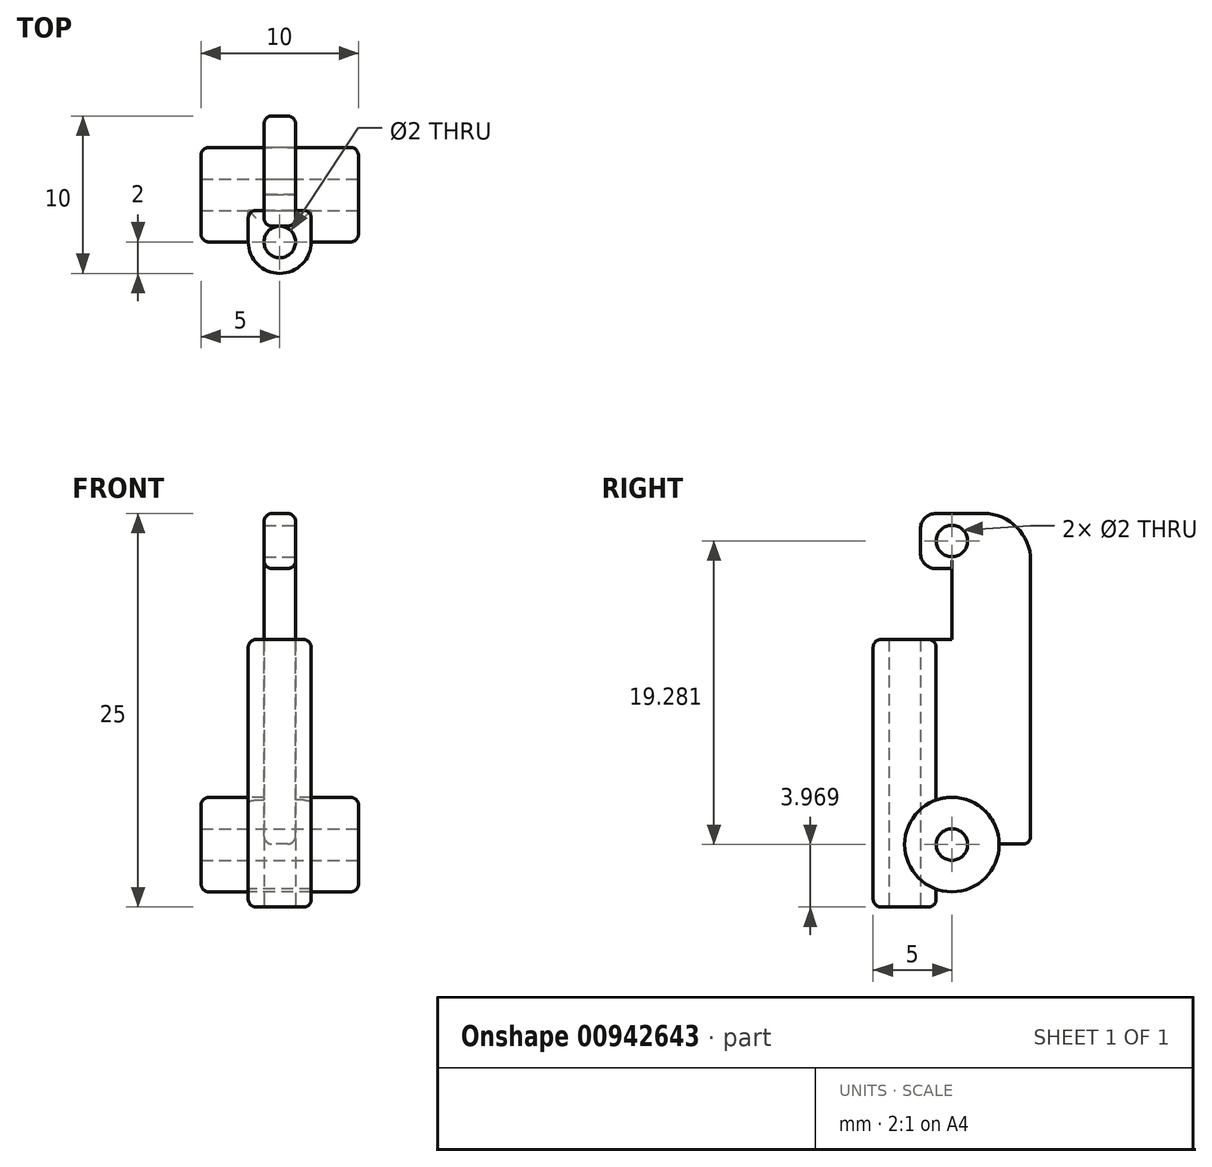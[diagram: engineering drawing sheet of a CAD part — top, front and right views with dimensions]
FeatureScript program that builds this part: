
annotation { "Feature Type Name" : "Feature", "Feature Type Description" : "" }
export const myFeature = defineFeature(function(context is Context, id is Id, definition is map)
    precondition{}
    {
        {
            var Q0;
            Q0=qCreatedBy(makeId("Front.planeOp"),FACE);
            var sketch = newSketch(context, id + "F0", { "sketchPlane" : qUnion([Q0])});
            skLineSegment(sketch, "E0.bottom", {"start": v(2, -8.5) * mm, "end": v(-2, -8.5) * mm});
            skLineSegment(sketch, "E0.top", {"start": v(2, 8.5) * mm, "end": v(-2, 8.5) * mm});
            skLineSegment(sketch, "E0.left", {"start": v(2, -8.5) * mm, "end": v(2, 8.5) * mm});
            skLineSegment(sketch, "E0.right", {"start": v(-2, -8.5) * mm, "end": v(-2, 8.5) * mm});
            skPoint(sketch, "E0.middle", {"position": v(0, 0) * mm});
            skSolve(sketch);
        }
        {
            var Q0;
            Q0 = qSketchRegion(id + "F0", true);
            extrude(context, id + "F1", {"entities" : qUnion([Q0]), "depth" : 4 * mm, "offsetDistance" : 25 * mm});
        }
        {
            var Q0;
            Q0=qCreatedBy(makeId("Right.planeOp"),FACE);
            var sketch = newSketch(context, id + "F2", { "sketchPlane" : qUnion([Q0])});
            skLineSegment(sketch, "E1.bottom", {"start": v(0, -4.5) * mm, "end": v(6, -4.5) * mm});
            skLineSegment(sketch, "E1.top", {"start": v(0, 16.5) * mm, "end": v(6, 16.5) * mm});
            skLineSegment(sketch, "E1.left", {"start": v(0, -4.5) * mm, "end": v(0, 16.5) * mm});
            skLineSegment(sketch, "E1.right", {"start": v(6, -4.5) * mm, "end": v(6, 16.5) * mm});
            skSolve(sketch);
        }
        {
            var Q0;
            Q0 = qSketchRegion(id + "F2", true);
            extrude(context, id + "F3", {"entities" : qUnion([Q0]), "operationType" : NewBodyOperationType.ADD, "depth" : 1 * mm, "offsetDistance" : 25 * mm});
        }
        {
            var Q0;
            Q0=qCreatedBy(makeId("Right.planeOp"),FACE);
            var sketch = newSketch(context, id + "F4", { "sketchPlane" : qUnion([Q0])});
            skLineSegment(sketch, "E2.bottom", {"start": v(0, -4.5) * mm, "end": v(6, -4.5) * mm});
            skLineSegment(sketch, "E2.top", {"start": v(0, 16.5) * mm, "end": v(6, 16.5) * mm});
            skLineSegment(sketch, "E2.left", {"start": v(0, -4.5) * mm, "end": v(0, 16.5) * mm});
            skLineSegment(sketch, "E2.right", {"start": v(6, -4.5) * mm, "end": v(6, 16.5) * mm});
            skSolve(sketch);
        }
        {
            var Q0;
            Q0 = qSketchRegion(id + "F4", true);
            extrude(context, id + "F5", {"entities" : qUnion([Q0]), "operationType" : NewBodyOperationType.ADD, "oppositeDirection" : true, "depth" : 1 * mm, "offsetDistance" : 25 * mm});
        }
        {
            var Q0;
            Q0=qCreatedBy(makeId("Right.planeOp"),FACE);
            var sketch = newSketch(context, id + "F6", { "sketchPlane" : qUnion([Q0])});
            skCircle(sketch, "E3", {"center": v(1, -4.53) * mm, "radius": 3 * mm});
            skSolve(sketch);
        }
        {
            var Q0;
            Q0=makeQuery(id+"F6.imprint","IMPRINT",FACE,{"disambiguationData":[TD([[makeQuery(id+"F6.imprint","IMPRINT",EDGE,{"derivedFrom":sQuery(id+"F6.wireOp",EDGE,"E3")}),1.0]])]});
            extrude(context, id + "F7", {"entities" : qUnion([Q0]), "operationType" : NewBodyOperationType.ADD, "depth" : 5 * mm, "offsetDistance" : 25 * mm});
        }
        {
            var Q0;
            Q0=makeQuery(id+"F7.opExtrude","CAP_FACE",FACE,{"disambiguationData":[OSD([sQuery(id+"F6.wireOp",EDGE,"E3")])],"isStart":false});
            extrude(context, id + "F8", {"entities" : qUnion([Q0]), "operationType" : NewBodyOperationType.ADD, "oppositeDirection" : true, "depth" : 10 * mm, "offsetDistance" : 25 * mm});
        }
        {
            var Q0;
            Q0=makeQuery(id+"F5.boolean.opBoolean","MERGE",FACE,{"derivedFrom":[makeQuery(id+"F3.opExtrude","SWEPT_FACE",FACE,{"disambiguationData":[OSD([sQuery(id+"F2.wireOp",EDGE,"E1.left")])]}),makeQuery(id+"F5.opExtrude","SWEPT_FACE",FACE,{"disambiguationData":[OSD([sQuery(id+"F4.wireOp",EDGE,"E2.left")])]})]});
            var sketch = newSketch(context, id + "F9", { "sketchPlane" : qUnion([Q0])});
            skLineSegment(sketch, "E4.bottom", {"start": v(-1, 8.5) * mm, "end": v(1, 8.5) * mm});
            skLineSegment(sketch, "E4.top", {"start": v(-1, 13) * mm, "end": v(1, 13) * mm});
            skLineSegment(sketch, "E4.left", {"start": v(-1, 8.5) * mm, "end": v(-1, 13) * mm});
            skLineSegment(sketch, "E4.right", {"start": v(1, 8.5) * mm, "end": v(1, 13) * mm});
            skSolve(sketch);
        }
        {
            var Q0;
            Q0 = qSketchRegion(id + "F9", true);
            extrude(context, id + "F10", {"entities" : qUnion([Q0]), "operationType" : NewBodyOperationType.REMOVE, "oppositeDirection" : true, "depth" : 1 * mm, "offsetDistance" : 25 * mm});
        }
        {
            var Q0;
            Q0=makeQuery(id+"F5.boolean.opBoolean","MERGE",FACE,{"derivedFrom":[makeQuery(id+"F3.opExtrude","SWEPT_FACE",FACE,{"disambiguationData":[OSD([sQuery(id+"F2.wireOp",EDGE,"E1.left")])]}),makeQuery(id+"F5.opExtrude","SWEPT_FACE",FACE,{"disambiguationData":[OSD([sQuery(id+"F4.wireOp",EDGE,"E2.left")])]})]});
            extrude(context, id + "F11", {"entities" : qUnion([Q0]), "operationType" : NewBodyOperationType.ADD, "depth" : 1 * mm, "offsetDistance" : 25 * mm});
        }
        {
            var Q0;
            Q0=makeQuery(id+"F5.boolean.opBoolean","MERGE",EDGE,{"derivedFrom":[makeQuery(id+"F3.opExtrude","SWEPT_EDGE",EDGE,{"disambiguationData":[OSD([sQuery(id+"F2.wireOp",EDGE,"E1.top"),sQuery(id+"F2.wireOp",EDGE,"E1.right")])]}),makeQuery(id+"F5.opExtrude","SWEPT_EDGE",EDGE,{"disambiguationData":[OSD([sQuery(id+"F4.wireOp",EDGE,"E2.top"),sQuery(id+"F4.wireOp",EDGE,"E2.right")])]})]});
            fillet(context, id + "F12", {"entities" : qUnion([Q0]), "radius" : 3 * mm, "tangentPropagation" : true, "allowEdgeOverflow" : false});
        }
        {
            var Q0;
            Q0=makeQuery(id+"F11.opExtrude","CAP_EDGE",EDGE,{"disambiguationData":[OSD([sQuery(id+"F9.wireOp",EDGE,"E4.top")])],"isStart":false});
            var Q1;
            Q1=makeQuery(id+"F11.opExtrude","CAP_EDGE",EDGE,{"disambiguationData":[OSD([sQuery(id+"F2.wireOp",EDGE,"E1.top"),sQuery(id+"F2.wireOp",EDGE,"E1.left"),sQuery(id+"F4.wireOp",EDGE,"E2.top"),sQuery(id+"F4.wireOp",EDGE,"E2.left")])],"isStart":false});
            fillet(context, id + "F13", {"entities" : qUnion([Q0, Q1]), "radius" : 1 * mm, "tangentPropagation" : true, "allowEdgeOverflow" : false});
        }
        {
            var Q0;
            Q0=makeQuery(id+"F1.opExtrude","CAP_EDGE",EDGE,{"disambiguationData":[OSD([sQuery(id+"F0.wireOp",EDGE,"E0.left")])],"isStart":false});
            var Q1;
            Q1=makeQuery(id+"F1.opExtrude","CAP_EDGE",EDGE,{"disambiguationData":[OSD([sQuery(id+"F0.wireOp",EDGE,"E0.right")])],"isStart":false});
            fillet(context, id + "F14", {"entities" : qUnion([Q0, Q1]), "radius" : 2 * mm, "tangentPropagation" : true, "allowEdgeOverflow" : false});
        }
        {
            var Q0;
            Q0=makeQuery(id+"F14.opFillet","BLEND_EDGE",EDGE,{"blendedFrom":[makeQuery(id+"F1.opExtrude","CAP_EDGE",EDGE,{"disambiguationData":[OSD([sQuery(id+"F0.wireOp",EDGE,"E0.left")])],"isStart":false}),makeQuery(id+"F10.boolean.opBoolean","MERGE",FACE,{"derivedFrom":[makeQuery(id+"F1.opExtrude","SWEPT_FACE",FACE,{"disambiguationData":[OSD([sQuery(id+"F0.wireOp",EDGE,"E0.top")])]})],"fromTools":[makeQuery(id+"F10.opExtrude","SWEPT_FACE",FACE,{"disambiguationData":[OSD([sQuery(id+"F9.wireOp",EDGE,"E4.bottom")])]})]})],"blendedInto":[makeQuery(id+"F10.boolean.opBoolean","MERGE",FACE,{"derivedFrom":[makeQuery(id+"F1.opExtrude","SWEPT_FACE",FACE,{"disambiguationData":[OSD([sQuery(id+"F0.wireOp",EDGE,"E0.top")])]})],"fromTools":[makeQuery(id+"F10.opExtrude","SWEPT_FACE",FACE,{"disambiguationData":[OSD([sQuery(id+"F9.wireOp",EDGE,"E4.bottom")])]})]})]});
            var Q1;
            Q1=makeQuery(id+"F10.boolean.opBoolean","COPY",EDGE,{"derivedFrom":makeQuery(id+"F10.opExtrude","CAP_EDGE",EDGE,{"disambiguationData":[OSD([sQuery(id+"F9.wireOp",EDGE,"E4.right")])],"isStart":false})});
            var Q2;
            Q2=makeQuery(id+"F10.boolean.opBoolean","COPY",EDGE,{"derivedFrom":makeQuery(id+"F10.opExtrude","CAP_EDGE",EDGE,{"disambiguationData":[OSD([sQuery(id+"F9.wireOp",EDGE,"E4.left")])],"isStart":false})});
            var Q3;
            {var subQ0=sQuery(id+"F0.wireOp",EDGE,"E0.left");var subQ1=sQuery(id+"F0.wireOp",EDGE,"E0.top");Q3=makeQuery(id+"F7.boolean.opBoolean","SPLIT",EDGE,{"disambiguationData":[TD([makeQuery(id+"F1.opExtrude","SWEPT_FACE",FACE,{"disambiguationData":[OSD([subQ1])]})])],"derivedFrom":makeQuery(id+"F1.opExtrude","CAP_EDGE",EDGE,{"disambiguationData":[OSD([subQ0])],"isStart":true})});}
            var Q4;
            {var subQ0=sQuery(id+"F0.wireOp",EDGE,"E0.right");var subQ1=sQuery(id+"F0.wireOp",EDGE,"E0.top");Q4=makeQuery(id+"F8.boolean.opBoolean","SPLIT",EDGE,{"disambiguationData":[TD([makeQuery(id+"F1.opExtrude","SWEPT_FACE",FACE,{"disambiguationData":[OSD([subQ1])]})])],"derivedFrom":makeQuery(id+"F1.opExtrude","CAP_EDGE",EDGE,{"disambiguationData":[OSD([subQ0])],"isStart":true})});}
            var Q5;
            Q5=makeQuery(id+"F14.opFillet","BLEND_EDGE",EDGE,{"blendedFrom":[makeQuery(id+"F1.opExtrude","CAP_EDGE",EDGE,{"disambiguationData":[OSD([sQuery(id+"F0.wireOp",EDGE,"E0.left")])],"isStart":false}),makeQuery(id+"F1.opExtrude","SWEPT_FACE",FACE,{"disambiguationData":[OSD([sQuery(id+"F0.wireOp",EDGE,"E0.bottom")])]})],"blendedInto":[makeQuery(id+"F1.opExtrude","SWEPT_FACE",FACE,{"disambiguationData":[OSD([sQuery(id+"F0.wireOp",EDGE,"E0.bottom")])]})]});
            var Q6;
            Q6=makeQuery(id+"F1.opExtrude","SWEPT_EDGE",EDGE,{"disambiguationData":[OSD([sQuery(id+"F0.wireOp",EDGE,"E0.bottom"),sQuery(id+"F0.wireOp",EDGE,"E0.left")])]});
            var Q7;
            Q7=makeQuery(id+"F1.opExtrude","CAP_EDGE",EDGE,{"disambiguationData":[OSD([sQuery(id+"F0.wireOp",EDGE,"E0.bottom")])],"isStart":true});
            fillet(context, id + "F15", {"entities" : qUnion([Q0, Q1, Q2, Q3, Q4, Q5, Q6, Q7]), "radius" : .5 * mm, "tangentPropagation" : true, "allowEdgeOverflow" : false});
        }
        {
            var Q0;
            Q0=makeQuery(id+"F5.opExtrude","CAP_EDGE",EDGE,{"disambiguationData":[OSD([sQuery(id+"F4.wireOp",EDGE,"E2.right")])],"isStart":false});
            var Q1;
            Q1=makeQuery(id+"F3.opExtrude","CAP_EDGE",EDGE,{"disambiguationData":[OSD([sQuery(id+"F2.wireOp",EDGE,"E1.right")])],"isStart":false});
            var Q2;
            Q2=makeQuery(id+"F10.boolean.opBoolean","COPY",EDGE,{"derivedFrom":makeQuery(id+"F10.opExtrude","SWEPT_EDGE",EDGE,{"disambiguationData":[OSD([sQuery(id+"F9.wireOp",EDGE,"E4.bottom"),sQuery(id+"F9.wireOp",EDGE,"E4.left")])]})});
            var Q3;
            Q3=makeQuery(id+"F10.boolean.opBoolean","COPY",EDGE,{"derivedFrom":makeQuery(id+"F10.opExtrude","SWEPT_EDGE",EDGE,{"disambiguationData":[OSD([sQuery(id+"F9.wireOp",EDGE,"E4.bottom"),sQuery(id+"F9.wireOp",EDGE,"E4.right")])]})});
            var Q4;
            {var subQ1=sQuery(id+"F0.wireOp",EDGE,"E0.top");var subQ2=makeQuery(id+"F1.opExtrude","SWEPT_FACE",FACE,{"disambiguationData":[OSD([subQ1])]});var subQ3=sQuery(id+"F0.wireOp",EDGE,"E0.left");var subQ4=makeQuery(id+"F1.opExtrude","CAP_FACE",FACE,{"disambiguationData":[OSD([sQuery(id+"F0.wireOp",EDGE,"E0.bottom"),subQ1,subQ3,sQuery(id+"F0.wireOp",EDGE,"E0.right")])],"isStart":true});Q4=makeQuery(id+"F3.boolean.opBoolean","SPLIT",EDGE,{"disambiguationData":[topologyDisambiguationEdgeConnected([subQ4,subQ2]),TD([makeQuery(id+"F1.opExtrude","SWEPT_FACE",FACE,{"disambiguationData":[OSD([subQ3])]})])],"derivedFrom":makeQuery(id+"F1.opExtrude","CAP_EDGE",EDGE,{"disambiguationData":[OSD([subQ1])],"isStart":true})});}
            var Q5;
            {var subQ1=sQuery(id+"F0.wireOp",EDGE,"E0.right");var subQ2=sQuery(id+"F0.wireOp",EDGE,"E0.top");var subQ3=makeQuery(id+"F1.opExtrude","SWEPT_FACE",FACE,{"disambiguationData":[OSD([subQ2])]});var subQ4=makeQuery(id+"F1.opExtrude","CAP_FACE",FACE,{"disambiguationData":[OSD([sQuery(id+"F0.wireOp",EDGE,"E0.bottom"),subQ2,sQuery(id+"F0.wireOp",EDGE,"E0.left"),subQ1])],"isStart":true});Q5=makeQuery(id+"F5.boolean.opBoolean","SPLIT",EDGE,{"derivedFrom":makeQuery(id+"F3.boolean.opBoolean","SPLIT",EDGE,{"disambiguationData":[topologyDisambiguationEdgeConnected([subQ4,subQ3]),TD([makeQuery(id+"F1.opExtrude","SWEPT_FACE",FACE,{"disambiguationData":[OSD([subQ1])]})])],"derivedFrom":makeQuery(id+"F1.opExtrude","CAP_EDGE",EDGE,{"disambiguationData":[OSD([subQ2])],"isStart":true})})});}
            fillet(context, id + "F16", {"entities" : qUnion([Q0, Q1, Q2, Q3, Q4, Q5]), "radius" : .5 * mm, "tangentPropagation" : true, "allowEdgeOverflow" : false});
        }
        {
            var Q0;
            Q0=makeQuery(id+"F5.opExtrude","CAP_EDGE",EDGE,{"disambiguationData":[OSD([sQuery(id+"F4.wireOp",EDGE,"E2.bottom")])],"isStart":false});
            var Q1;
            Q1=makeQuery(id+"F8.opExtrude","CAP_EDGE",EDGE,{"disambiguationData":[OSD([sQuery(id+"F6.wireOp",EDGE,"E3")])],"isStart":false});
            fillet(context, id + "F17", {"entities" : qUnion([Q0, Q1]), "radius" : .5 * mm, "tangentPropagation" : true, "allowEdgeOverflow" : false});
        }
        {
            var Q0;
            Q0=makeQuery(id+"F7.opExtrude","CAP_EDGE",EDGE,{"disambiguationData":[OSD([sQuery(id+"F6.wireOp",EDGE,"E3")])],"isStart":false});
            fillet(context, id + "F18", {"entities" : qUnion([Q0]), "radius" : .5 * mm, "tangentPropagation" : true, "allowEdgeOverflow" : false});
        }
        {
            var Q0;
            Q0=makeQuery(id+"F1.opExtrude","SWEPT_FACE",FACE,{"disambiguationData":[OSD([sQuery(id+"F0.wireOp",EDGE,"E0.bottom")])]});
            var sketch = newSketch(context, id + "F19", { "sketchPlane" : qUnion([Q0])});
            skCircle(sketch, "E5", {"center": v(0, 2) * mm, "radius": 1 * mm});
            skSolve(sketch);
        }
        {
            var Q0;
            Q0 = qSketchRegion(id + "F19", true);
            extrude(context, id + "F20", {"entities" : qUnion([Q0]), "operationType" : NewBodyOperationType.REMOVE, "oppositeDirection" : true, "depth" : 17 * mm, "offsetDistance" : 25 * mm});
        }
        {
            var Q0;
            Q0=makeQuery(id+"F7.opExtrude","CAP_FACE",FACE,{"disambiguationData":[OSD([sQuery(id+"F6.wireOp",EDGE,"E3")])],"isStart":false});
            var sketch = newSketch(context, id + "F21", { "sketchPlane" : qUnion([Q0])});
            skCircle(sketch, "E6", {"center": v(1, -4.53) * mm, "radius": 1 * mm});
            skSolve(sketch);
        }
        {
            var Q0;
            Q0 = qSketchRegion(id + "F21", true);
            extrude(context, id + "F22", {"entities" : qUnion([Q0]), "operationType" : NewBodyOperationType.REMOVE, "oppositeDirection" : true, "depth" : 10 * mm, "offsetDistance" : 25 * mm});
        }
        {
            var Q0;
            {var subQ0=sQuery(id+"F2.wireOp",EDGE,"E1.left");Q0=makeQuery(id+"F11.boolean.opBoolean","MERGE",FACE,{"derivedFrom":[makeQuery(id+"F3.opExtrude","CAP_FACE",FACE,{"disambiguationData":[OSD([sQuery(id+"F2.wireOp",EDGE,"E1.bottom"),sQuery(id+"F2.wireOp",EDGE,"E1.top"),subQ0,sQuery(id+"F2.wireOp",EDGE,"E1.right")])],"isStart":false}),makeQuery(id+"F11.opExtrude","SWEPT_FACE",FACE,{"disambiguationData":[OSD([subQ0])]})]});}
            var sketch = newSketch(context, id + "F23", { "sketchPlane" : qUnion([Q0])});
            skCircle(sketch, "E7", {"center": v(1, 14.75) * mm, "radius": 1 * mm});
            skSolve(sketch);
        }
        {
            var Q0;
            Q0 = qSketchRegion(id + "F23", true);
            extrude(context, id + "F24", {"entities" : qUnion([Q0]), "operationType" : NewBodyOperationType.REMOVE, "oppositeDirection" : true, "depth" : 2 * mm, "offsetDistance" : 25 * mm});
        }
    });
